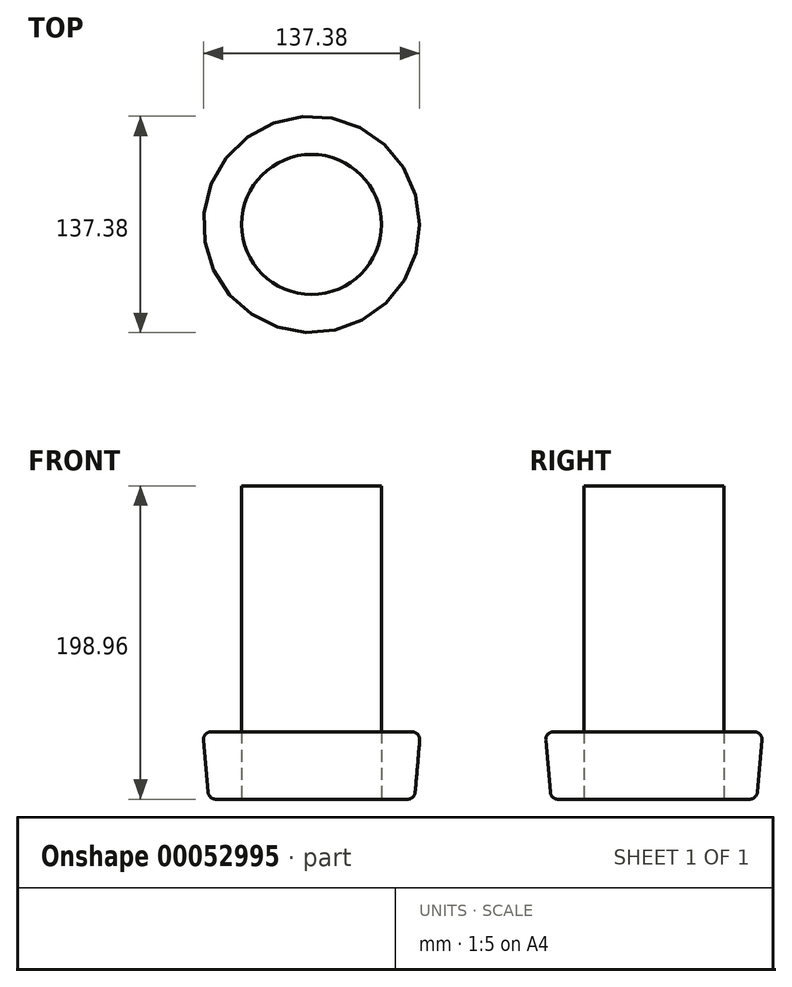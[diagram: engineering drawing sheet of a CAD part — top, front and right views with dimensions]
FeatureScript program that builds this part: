
annotation { "Feature Type Name" : "Feature", "Feature Type Description" : "" }
export const myFeature = defineFeature(function(context is Context, id is Id, definition is map)
    precondition{}
    {
        {
            var Q0;
            Q0=qCreatedBy(makeId("Top.planeOp"),FACE);
            var sketch = newSketch(context, id + "F0", { "sketchPlane" : qUnion([Q0])});
            skCircle(sketch, "E0", {"center": v(0, 0) * mm, "radius": 65.4 * mm});
            skSolve(sketch);
        }
        {
            var Q0;
            Q0=qCreatedBy(makeId("Top.planeOp"),FACE);
            var sketch = newSketch(context, id + "F1", { "sketchPlane" : qUnion([Q0])});
            skCircle(sketch, "E1", {"center": v(0, 0) * mm, "radius": 44.45 * mm});
            skSolve(sketch);
        }
        {
            var Q0;
            Q0=makeQuery(id+"F0.imprint","IMPRINT",FACE,{"disambiguationData":[TD([[makeQuery(id+"F0.imprint","IMPRINT",EDGE,{"derivedFrom":sQuery(id+"F0.wireOp",EDGE,"E0")}),1.0]])]});
            extrude(context, id + "F2", {"entities" : qUnion([Q0]), "depth" : 42.88 * mm, "hasDraft" : true, "draftAngle" : 5 * degree});
        }
        {
            var Q0;
            Q0=makeQuery(id+"F2.opExtrude","CAP_EDGE",EDGE,{"disambiguationData":[OSD([sQuery(id+"F0.wireOp",EDGE,"E0")])],"isStart":true});
            var Q1;
            Q1=makeQuery(id+"F2.opExtrude","CAP_EDGE",EDGE,{"disambiguationData":[OSD([sQuery(id+"F0.wireOp",EDGE,"E0")])],"isStart":false});
            fillet(context, id + "F3", {"entities" : qUnion([Q0, Q1]), "radius" : 5.08 * mm, "tangentPropagation" : true, "allowEdgeOverflow" : false});
        }
        {
            var Q0;
            Q0=makeQuery(id+"F1.imprint","IMPRINT",FACE,{"disambiguationData":[TD([[makeQuery(id+"F1.imprint","IMPRINT",EDGE,{"derivedFrom":sQuery(id+"F1.wireOp",EDGE,"E1")}),1.0]])]});
            extrude(context, id + "F4", {"entities" : qUnion([Q0]), "endBound" : BoundingType.THROUGH_ALL, "depth" : 25.4 * mm});
        }
    });
